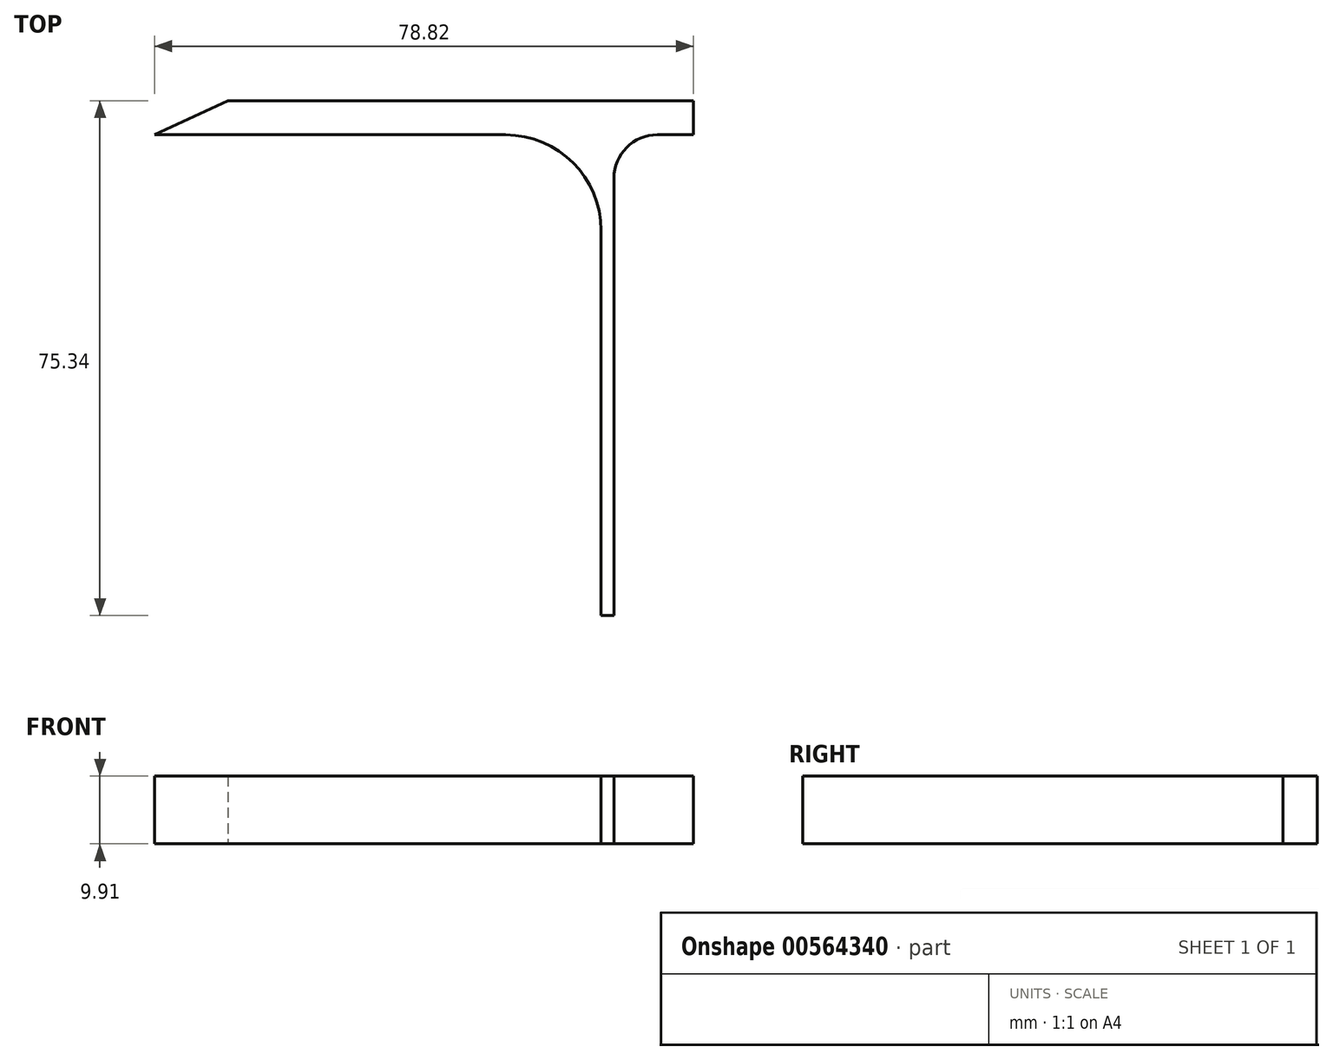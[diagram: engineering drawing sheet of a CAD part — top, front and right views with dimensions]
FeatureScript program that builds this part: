
annotation { "Feature Type Name" : "Feature", "Feature Type Description" : "" }
export const myFeature = defineFeature(function(context is Context, id is Id, definition is map)
    precondition{}
    {
        {
            var Q0;
            Q0=qCreatedBy(makeId("Top.planeOp"),FACE);
            var sketch = newSketch(context, id + "F0", { "sketchPlane" : qUnion([Q0])});
            skPoint(sketch, "E0.visualSharp", {"position": v(-69.85, 79.19) * mm});
            skPoint(sketch, "E1.visualSharp", {"position": v(69.85, 79.19) * mm});
            skLineSegment(sketch, "E2.bottom", {"start": v(16.05, -44.2) * mm, "end": v(14.16, -44.2) * mm});
            skLineSegment(sketch, "E2.top", {"start": v(16.05, 31.15) * mm, "end": v(14.16, 31.15) * mm});
            skLineSegment(sketch, "E2.left", {"start": v(16.05, -44.2) * mm, "end": v(16.05, 19.8) * mm});
            skLineSegment(sketch, "E2.right", {"start": v(14.16, -44.2) * mm, "end": v(14.16, 12.18) * mm});
            skLineSegment(sketch, "E3.bottom", {"start": v(-40.45, 31.15) * mm, "end": v(27.66, 31.15) * mm});
            skLineSegment(sketch, "E3.top", {"start": v(-45.07, 26.15) * mm, "end": v(0.2, 26.15) * mm});
            skLineSegment(sketch, "E3.right", {"start": v(27.66, 31.15) * mm, "end": v(27.66, 26.15) * mm});
            skLineSegment(sketch, "E4.trimOffspring", {"start": v(22.4, 26.15) * mm, "end": v(27.66, 26.15) * mm});
            skPoint(sketch, "E5.visualSharp", {"position": v(16.05, 26.15) * mm});
            skArc(sketch, "E5.filletArc", {"start": v(22.4, 26.15) * mm, "mid": v(17.91, 24.3) * mm, "end": v(16.05, 19.8) * mm});
            skPoint(sketch, "E6.visualSharp", {"position": v(14.16, 26.15) * mm});
            skArc(sketch, "E6.filletArc", {"start": v(14.16, 12.18) * mm, "mid": v(10.07, 22.06) * mm, "end": v(0.2, 26.15) * mm});
            skLineSegment(sketch, "E7", {"start": v(-47.07, 26.15) * mm, "end": v(-45.07, 26.15) * mm});
            skPoint(sketch, "E8.orphan", {"position": v(-49.82, 26.15) * mm});
            skLineSegment(sketch, "E9", {"start": v(-51.16, 26.15) * mm, "end": v(-45.07, 26.15) * mm});
            skLineSegment(sketch, "E10", {"start": v(-51.16, 26.15) * mm, "end": v(-40.45, 31.15) * mm});
            skSolve(sketch);
        }
        {
            var Q0;
            Q0 = qSketchRegion(id + "F0", true);
            extrude(context, id + "F1", {"entities" : qUnion([Q0]), "depth" : 9.9 * mm, "offsetDistance" : 25.4 * mm});
        }
    });
